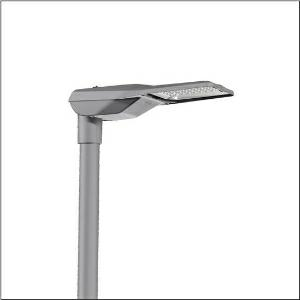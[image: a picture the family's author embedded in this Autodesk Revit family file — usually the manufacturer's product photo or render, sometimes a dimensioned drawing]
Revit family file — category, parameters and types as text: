
# Revit family: streetlight_sl_21_mini___st1_0a_5xe2d33s08gb_0caf
name_source: partatom
category: Lighting Fixtures
units: mm (PartAtom-declared; Revit-internal decimal feet)

## family parameters
Cut with Voids When Loaded = No
Host = Face
Light Source = No
Part Type = Normal
Room Calculation Point = No
Round Connector Dimension = Use Diameter
Shared = No

## types (1)
- --- (1 x LED, 5940 lm, 40.4 W, 3000K)
    Apparent Load = 40 VA
    CIE Flux Codes = 37 72 97 100 100
    Color Rendering = 70
    Color Temperature = 3000K
    Default Elevation = 1800 mm
    Description = Streetlight SL 21 mini, mast luminaire, primary light control with lens, of PMMA, primary optical cover: cover, of toughened safety glass, transparent, light distribution: ST1.0a, light emission: direct distribution, primary light characteristic: asymmetric, installation type: side-entry, post-top, LED, High Power LED, rated luminous flux: 5.940lm, luminous efficacy: 147lm/W, light colour: 730, colour temperature: 3000K, control gear: D4i, control: flexible luminous flux parameterisation, time-dependent luminous flux control, constant luminous flux control, overheat protection, pre-setting: logarithmic dimming characteristic, mains connection: 220..240V, AC, 50/60Hz, start of lifetime: 40W, end of service life: 41W, reduction: 19W, luminaire housing, of diecast aluminium, powder-coated, Siteco® metallic grey (DB 702S), corrosivity category C5 mid according to DIN EN ISO 12944, please order mast flange separately, inclination adjustable: 0°, 5°, 10°, 15°, sealing non-destructively replaceable, multi-level sealing system, length: 628mm, width: 235mm, height: 110mm, mast flange for spigot size: 42mm (side-entry): 5XC10008XM4, 60/48mm (side-entry/post-top): 5XC10108XM2, 76/60mm (side-entry/post-top): 5XC10108XM1, mounting height: 4..8m, Smart Interface above, protection rating (complete): IP66, insulation class (complete): insulation class II (safety insulation), certification: CE, ENEC, ENEC+, VDE, impact resistance: IK10, permissible operating ambient temperature for outdoor applications: -40..+50°C, standard-compliant lighting for roads and squares, packaging unit: 1 piece

Light Distribution: ST1.0a
    Height = 110 mm
    Lamp = 1 x LED
    Lamp Light Flux = 5940 lm
    Lamp Power = 40.4 W
    Lamp count = 1
    Length = 625 mm
    Luminous efficacy = 147 lm/W
    Manufacturer = Siteco
    ModVariant = No
    Model = 5XE2D33S08GB
    Number of Poles = 1
    OnlyDefault = Yes
    Power Factor = 1
    Product Name = Streetlight SL 21 mini | ST1.0a
    Product group = mast luminaire | pylon top
    ProductGroupID = 6100
    Protection Class = Protection class II
    Protection Degree = IP 66
    RLX_Detail_Level = 1
    RLX_Emergency_Light_Flux = 0 lm
    RLX_Emergency_Type = 0
    RLX_Emergency_Type_DB = No
    RlxData = <blob elided: 26093 chars, md5=98f01db9>
    Socket = socket
    Standby Power = 0 W
    System Light Flux = 5940 lm
    System Power = 40 W
    Type Comments = factory setting: luminous flux: 100 % | dim-lin: 254 | 812 mA
    Type Image = l_1003515.jpg
    URL = http://relux.com
    VarID = @adj_188728
    Voltage = 0 V
    Weight = 0.00 kg
    Width = 234 mm

## geometry (parser evidence)
native form markers: Blend x4, Sweep x11
no freeform markers — native parametric forms only
